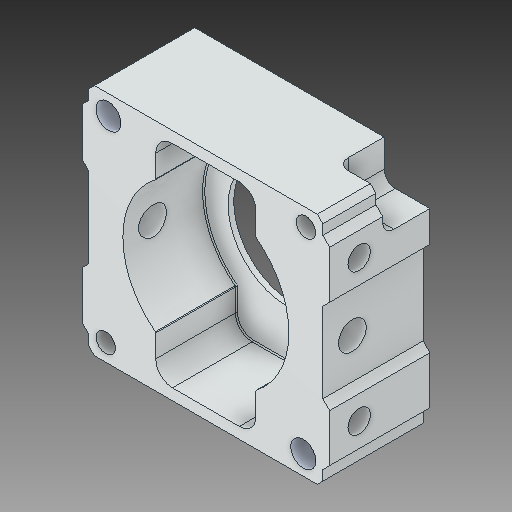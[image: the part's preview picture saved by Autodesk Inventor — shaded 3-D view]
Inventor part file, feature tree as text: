
AUTODESK INVENTOR PART (.ipt)
format: ipt  version: 2018 (Build 220112000, 112)  size: 268,288 bytes
history: native  units: in
note: dims shown in document units (in); Inventor stores cm internally (conversion verified against a paired STEP export)
features: chamfer x1
ambient origin geometry x8: Origin, YZ Plane, XZ Plane, XY Plane, X Axis, Y Axis, Z Axis, Center Point
bodies: Solid1 (feature_tree)
feature tree (1):
  chamfer  "Chamfer4"  [1 undecoded]
note: 1 required parameter value undecoded (feature->parameter linkage not recoverable at this tier; creation-order binding heuristic only, values carry confidence <= 0.55)
